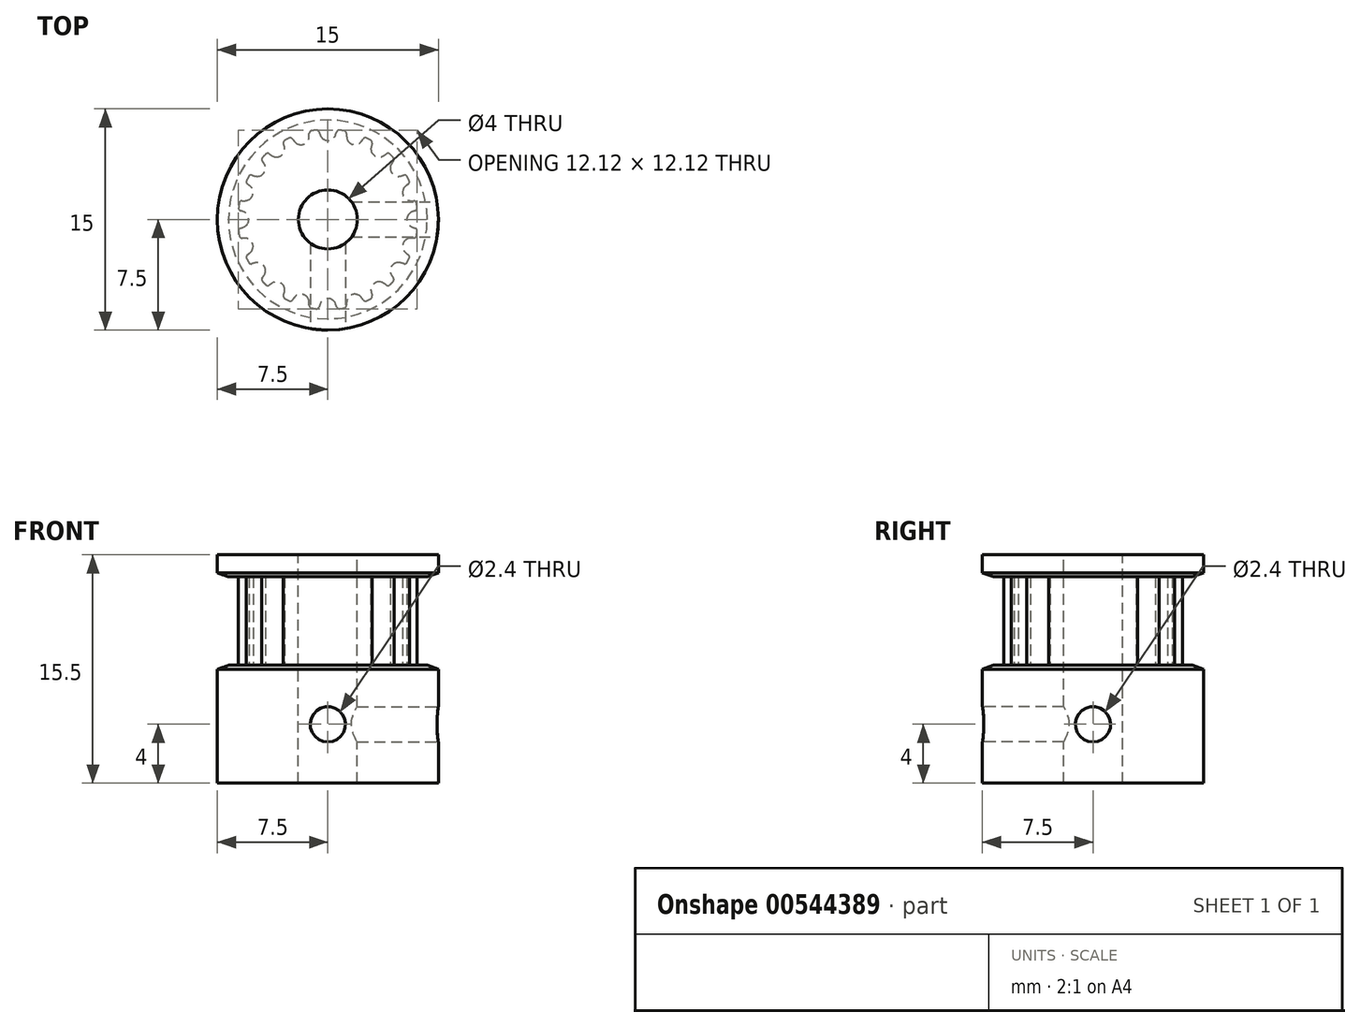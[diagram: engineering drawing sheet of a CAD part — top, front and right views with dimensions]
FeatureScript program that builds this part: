
annotation { "Feature Type Name" : "Feature", "Feature Type Description" : "" }
export const myFeature = defineFeature(function(context is Context, id is Id, definition is map)
    precondition{}
    {
        {
            assignVariable(context, id + "F0", {"name" : "teeth", "anyValue" : 20});
        }
        {
            assignVariable(context, id + "F1", {"name" : "belt_width", "anyValue" : 6 * mm});
        }
        {
            assignVariable(context, id + "F2", {"name" : "bore_diameter", "anyValue" : 4 * mm});
        }
        {
            var Q0;
            Q0=qCreatedBy(makeId("Top.planeOp"),FACE);
            var sketch = newSketch(context, id + "F3", { "sketchPlane" : qUnion([Q0])});
            skLineSegment(sketch, "E0", {"start": v(0, 0) * mm, "end": v(0, 5.36) * mm, "construction": true});
            skCircle(sketch, "E1", {"center": v(0, 0) * mm, "radius": 6.11 * mm});
            skPoint(sketch, "E2.MirrorCS.end.orphan", {"position": v(0.96, 6.04) * mm});
            skLineSegment(sketch, "E3", {"start": v(0.96, 6.04) * mm, "end": v(1, 6.29) * mm, "construction": true});
            skLineSegment(sketch, "E4", {"start": v(-0.96, 6.04) * mm, "end": v(-1, 6.29) * mm, "construction": true});
            skArc(sketch, "E5", {"start": v(0, 5.36) * mm, "mid": v(0.31, 5.46) * mm, "end": v(0.52, 5.72) * mm});
            skArc(sketch, "E6", {"start": v(0.52, 5.72) * mm, "mid": v(0.56, 5.83) * mm, "end": v(0.58, 5.94) * mm, "construction": true});
            skLineSegment(sketch, "E7", {"start": v(0, 5.36) * mm, "end": v(0, 6.11) * mm, "construction": true});
            skLineSegment(sketch, "E8", {"start": v(0, 6.11) * mm, "end": v(0, 6.37) * mm, "construction": true});
            skArc(sketch, "E9", {"start": v(0.58, 5.94) * mm, "mid": v(0.64, 6.04) * mm, "end": v(0.75, 6.07) * mm, "construction": true});
            skArc(sketch, "E10", {"start": v(1, 6.29) * mm, "mid": v(0, 6.37) * mm, "end": v(-1, 6.29) * mm, "construction": true});
            skLineSegment(sketch, "E11", {"start": v(0.96, 6.04) * mm, "end": v(0.84, 5.3) * mm});
            skLineSegment(sketch, "E12", {"start": v(0.84, 5.3) * mm, "end": v(0, 0) * mm});
            skLineSegment(sketch, "E13", {"start": v(0, 0) * mm, "end": v(-0.84, 5.3) * mm});
            skLineSegment(sketch, "E14", {"start": v(-0.84, 5.3) * mm, "end": v(-0.96, 6.04) * mm});
            skArc(sketch, "E15", {"start": v(0.8, 6.06) * mm, "mid": v(0.67, 6.03) * mm, "end": v(0.6, 5.93) * mm});
            skArc(sketch, "E16", {"start": v(0.52, 5.72) * mm, "mid": v(0.56, 5.83) * mm, "end": v(0.6, 5.93) * mm});
            skArc(sketch, "E17.MirrorCS", {"start": v(0, 5.36) * mm, "mid": v(-0.31, 5.46) * mm, "end": v(-0.52, 5.72) * mm});
            skArc(sketch, "E18.MirrorCS", {"start": v(-0.52, 5.72) * mm, "mid": v(-0.56, 5.83) * mm, "end": v(-0.6, 5.93) * mm});
            skArc(sketch, "E19.MirrorCS", {"start": v(-0.8, 6.06) * mm, "mid": v(-0.67, 6.03) * mm, "end": v(-0.6, 5.93) * mm});
            skArc(sketch, "E20", {"start": v(0, 6.11) * mm, "mid": v(-0.2, 6.1) * mm, "end": v(-0.4, 6.1) * mm});
            skArc(sketch, "E21", {"start": v(0.84, 5.3) * mm, "mid": v(0, 5.36) * mm, "end": v(-0.84, 5.3) * mm, "construction": true});
            skLineSegment(sketch, "E22", {"start": v(1, 6.29) * mm, "end": v(1.05, 6.66) * mm, "construction": true});
            skLineSegment(sketch, "E23", {"start": v(-1, 6.29) * mm, "end": v(-1.05, 6.66) * mm, "construction": true});
            skArc(sketch, "E24", {"start": v(-1.05, 6.66) * mm, "mid": v(0, 6.74) * mm, "end": v(1.05, 6.66) * mm, "construction": true});
            skSolve(sketch);
        }
        {
            var Q0;
            Q0=makeQuery(id+"F3.imprint","IMPRINT",FACE,{"disambiguationData":[TD([[makeQuery(id+"F3.imprint","IMPRINT",EDGE,{"derivedFrom":sQuery(id+"F3.wireOp",EDGE,"E5")}),-1.0]])]});
            var Q1;
            {var subQ1=sQuery(id+"F3.wireOp",EDGE,"E14");Q1=makeQuery(id+"F3.imprint","IMPRINT",FACE,{"disambiguationData":[TD([[makeQuery(id+"F3.imprint","IMPRINT",EDGE,{"derivedFrom":subQ1}),-1.0]])]});}
            var Q2;
            {var subQ0=sQuery(id+"F3.wireOp",EDGE,"E12");Q2=makeQuery(id+"F3.imprint","IMPRINT",FACE,{"disambiguationData":[TD([[makeQuery(id+"F3.imprint","IMPRINT",EDGE,{"derivedFrom":subQ0}),-1.0]])]});}
            extrude(context, id + "F4", {"entities" : qUnion([Q0, Q1, Q2]), "depth" : getVariable(context, 'belt_width'), "symmetric" : true});
        }
        {
            var Q0;
            Q0=makeQuery(id+"F4.opExtrude","SWEPT_BODY",BODY,{"disambiguationData":[OSD([sQuery(id+"F3.wireOp",EDGE,"E1"),sQuery(id+"F3.wireOp",EDGE,"E5"),sQuery(id+"F3.wireOp",EDGE,"E11"),sQuery(id+"F3.wireOp",EDGE,"E12"),sQuery(id+"F3.wireOp",EDGE,"E13"),sQuery(id+"F3.wireOp",EDGE,"E14"),sQuery(id+"F3.wireOp",EDGE,"E15"),sQuery(id+"F3.wireOp",EDGE,"E16"),sQuery(id+"F3.wireOp",EDGE,"E17.MirrorCS"),sQuery(id+"F3.wireOp",EDGE,"E18.MirrorCS"),sQuery(id+"F3.wireOp",EDGE,"E19.MirrorCS")])]});
            var Q1;
            Q1=makeQuery(id+"F4.opExtrude","SWEPT_EDGE",EDGE,{"disambiguationData":[OSD([sQuery(id+"F3.wireOp",EDGE,"E12"),sQuery(id+"F3.wireOp",EDGE,"E13")])]});
            circularPattern(context, id + "F5", {"operationType" : NewBodyOperationType.ADD, "entities" : qUnion([Q0]), "axis" : qUnion([Q1]), "angle" : 360 * degree, "instanceCount" : getVariable(context, 'teeth'), "equalSpace" : true});
        }
        {
            var Q0;
            Q0=qCreatedBy(makeId("Front.planeOp"),FACE);
            var sketch = newSketch(context, id + "F6", { "sketchPlane" : qUnion([Q0])});
            skLineSegment(sketch, "E25", {"start": v(0, -3) * mm, "end": v(6.74, -3) * mm});
            skLineSegment(sketch, "E26", {"start": v(6.74, -3) * mm, "end": v(7.5, -3.28) * mm});
            skLineSegment(sketch, "E27", {"start": v(7.5, -3.28) * mm, "end": v(7.5, -11) * mm});
            skLineSegment(sketch, "E28", {"start": v(7.5, -11) * mm, "end": v(0, -11) * mm});
            skLineSegment(sketch, "E29", {"start": v(0, -11) * mm, "end": v(0, -3) * mm});
            skLineSegment(sketch, "E30", {"start": v(0, 3) * mm, "end": v(6.74, 3) * mm});
            skLineSegment(sketch, "E31", {"start": v(7.5, 3.28) * mm, "end": v(6.74, 3) * mm});
            skLineSegment(sketch, "E32", {"start": v(7.5, 3.28) * mm, "end": v(7.5, 4.5) * mm});
            skLineSegment(sketch, "E33", {"start": v(7.5, 4.5) * mm, "end": v(0, 4.5) * mm});
            skLineSegment(sketch, "E34", {"start": v(0, 4.5) * mm, "end": v(0, 3) * mm});
            skLineSegment(sketch, "E35", {"start": v(6.74, -3) * mm, "end": v(7.5, -3) * mm, "construction": true});
            skLineSegment(sketch, "E36", {"start": v(7.5, -3) * mm, "end": v(7.5, -3.28) * mm, "construction": true});
            skLineSegment(sketch, "E37", {"start": v(6.74, 3) * mm, "end": v(7.5, 3) * mm, "construction": true});
            skLineSegment(sketch, "E38", {"start": v(7.5, 3) * mm, "end": v(7.5, 3.28) * mm, "construction": true});
            skLineSegment(sketch, "E39", {"start": v(6.11, 0) * mm, "end": v(6.11, -3) * mm, "construction": true});
            skSolve(sketch);
        }
        {
            var Q0;
            Q0=qSketchRegion(id+"F6",true);
            var Q1;
            Q1=qConstructionFilter(qBodyType(qCreatedBy(id+"F6",EDGE),BodyType.WIRE),ConstructionObject.NO);
            var Q2;
            Q2=sQuery(id+"F6.wireOp",EDGE,"E29");
            revolve(context, id + "F7", {"operationType" : NewBodyOperationType.ADD, "entities" : qUnion([Q0]), "surfaceEntities" : qUnion([Q1]), "axis" : qUnion([Q2]), "revolveType" : RevolveType.FULL});
        }
        {
            var Q0;
            Q0=makeQuery(id+"F7.opRevolve","SWEPT_FACE",FACE,{"disambiguationData":[OSD([sQuery(id+"F6.wireOp",EDGE,"E28")])]});
            var sketch = newSketch(context, id + "F8", { "sketchPlane" : qUnion([Q0])});
            skPoint(sketch, "E40", {"position": v(0, 0) * mm});
            skSolve(sketch);
        }
        {
            var Q0;
            Q0=sQuery(id+"F8.wireOp",VERTEX,"E40");
            var Q1;
            Q1=makeQuery(id+"F4.opExtrude","SWEPT_BODY",BODY,{"disambiguationData":[OSD([sQuery(id+"F3.wireOp",EDGE,"E1"),sQuery(id+"F3.wireOp",EDGE,"E5"),sQuery(id+"F3.wireOp",EDGE,"E11"),sQuery(id+"F3.wireOp",EDGE,"E12"),sQuery(id+"F3.wireOp",EDGE,"E13"),sQuery(id+"F3.wireOp",EDGE,"E14"),sQuery(id+"F3.wireOp",EDGE,"E15"),sQuery(id+"F3.wireOp",EDGE,"E16"),sQuery(id+"F3.wireOp",EDGE,"E17.MirrorCS"),sQuery(id+"F3.wireOp",EDGE,"E18.MirrorCS"),sQuery(id+"F3.wireOp",EDGE,"E19.MirrorCS")])]});
            hole(context, id + "F9", {"style" : HoleStyle.SIMPLE, "holeDiameter" : getVariable(context, 'bore_diameter'), "endStyle" : HoleEndStyle.THROUGH, "locations" : qUnion([Q0]), "scope" : qUnion([Q1]), "isTappedThrough" : true, "startStyle" : HoleStartStyle.PART});
        }
        {
            var Q0;
            Q0=qCreatedBy(makeId("Front.planeOp"),FACE);
            var sketch = newSketch(context, id + "F10", { "sketchPlane" : qUnion([Q0])});
            skPoint(sketch, "E41", {"position": v(0, -7) * mm});
            skLineSegment(sketch, "E42", {"start": v(0, -11) * mm, "end": v(0, -3) * mm});
            skSolve(sketch);
        }
        {
            var Q0;
            Q0=qCreatedBy(makeId("Right.planeOp"),FACE);
            var sketch = newSketch(context, id + "F11", { "sketchPlane" : qUnion([Q0])});
            skPoint(sketch, "E43", {"position": v(0, -7) * mm});
            skSolve(sketch);
        }
        {
            var Q0;
            Q0=sQuery(id+"F10.wireOp",VERTEX,"E41");
            var Q1;
            Q1=makeQuery(id+"F4.opExtrude","SWEPT_BODY",BODY,{"disambiguationData":[OSD([sQuery(id+"F3.wireOp",EDGE,"E1"),sQuery(id+"F3.wireOp",EDGE,"E5"),sQuery(id+"F3.wireOp",EDGE,"E11"),sQuery(id+"F3.wireOp",EDGE,"E12"),sQuery(id+"F3.wireOp",EDGE,"E13"),sQuery(id+"F3.wireOp",EDGE,"E14"),sQuery(id+"F3.wireOp",EDGE,"E15"),sQuery(id+"F3.wireOp",EDGE,"E16"),sQuery(id+"F3.wireOp",EDGE,"E17.MirrorCS"),sQuery(id+"F3.wireOp",EDGE,"E18.MirrorCS"),sQuery(id+"F3.wireOp",EDGE,"E19.MirrorCS")])]});
            hole(context, id + "F12", {"style" : HoleStyle.SIMPLE, "endStyle" : HoleEndStyle.THROUGH, "oppositeDirection" : true, "standardTappedOrClearance" : lookupTablePath({ "standard" : "ISO", "engagement" : "75%", "pitch" : "0.6 mm", "size" : "M3", "type" : "Tapped" }), "standardBlindInLast" : lookupTablePath({ "standard" : "ISO", "engagement" : "75%", "pitch" : "0.6 mm", "size" : "M3", "type" : "Tapped" }), "holeDiameter" : 2.4 * mm, "locations" : qUnion([Q0]), "scope" : qUnion([Q1]), "isTappedThrough" : true, "showTappedDepth" : true, "startStyle" : HoleStartStyle.PART});
        }
        {
            var Q0;
            Q0=sQuery(id+"F11.wireOp",VERTEX,"E43");
            var Q1;
            Q1=makeQuery(id+"F4.opExtrude","SWEPT_BODY",BODY,{"disambiguationData":[OSD([sQuery(id+"F3.wireOp",EDGE,"E1"),sQuery(id+"F3.wireOp",EDGE,"E5"),sQuery(id+"F3.wireOp",EDGE,"E11"),sQuery(id+"F3.wireOp",EDGE,"E12"),sQuery(id+"F3.wireOp",EDGE,"E13"),sQuery(id+"F3.wireOp",EDGE,"E14"),sQuery(id+"F3.wireOp",EDGE,"E15"),sQuery(id+"F3.wireOp",EDGE,"E16"),sQuery(id+"F3.wireOp",EDGE,"E17.MirrorCS"),sQuery(id+"F3.wireOp",EDGE,"E18.MirrorCS"),sQuery(id+"F3.wireOp",EDGE,"E19.MirrorCS")])]});
            hole(context, id + "F13", {"style" : HoleStyle.SIMPLE, "endStyle" : HoleEndStyle.THROUGH, "oppositeDirection" : true, "standardTappedOrClearance" : lookupTablePath({ "standard" : "ISO", "engagement" : "75%", "pitch" : "0.6 mm", "size" : "M3", "type" : "Tapped" }), "standardBlindInLast" : lookupTablePath({ "standard" : "ISO", "engagement" : "75%", "pitch" : "0.6 mm", "size" : "M3", "type" : "Tapped" }), "holeDiameter" : 2.4 * mm, "locations" : qUnion([Q0]), "scope" : qUnion([Q1]), "isTappedThrough" : true, "showTappedDepth" : true, "startStyle" : HoleStartStyle.PART});
        }
    });
